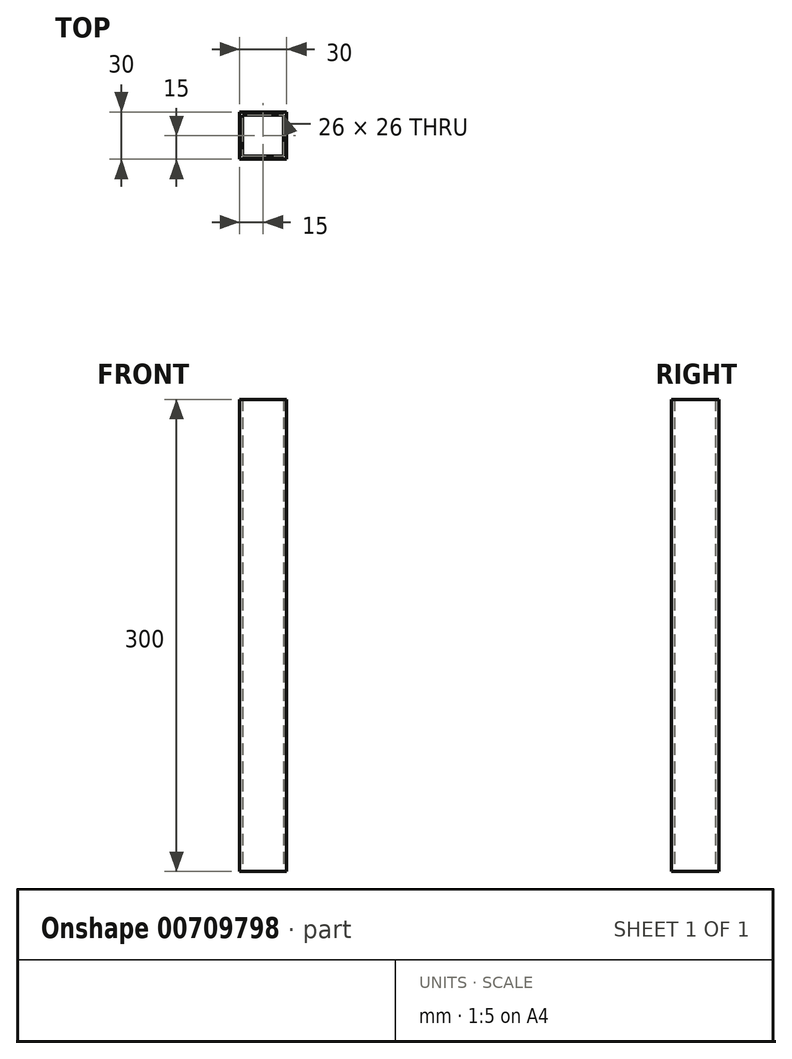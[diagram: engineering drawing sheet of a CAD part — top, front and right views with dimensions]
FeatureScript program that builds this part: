
annotation { "Feature Type Name" : "Feature", "Feature Type Description" : "" }
export const myFeature = defineFeature(function(context is Context, id is Id, definition is map)
    precondition{}
    {
        {
            var Q0;
            Q0=qCreatedBy(makeId("Top.planeOp"),FACE);
            var sketch = newSketch(context, id + "F0", { "sketchPlane" : qUnion([Q0])});
            skLineSegment(sketch, "E0.bottom", {"start": v(0, 0) * mm, "end": v(-30, 0) * mm});
            skLineSegment(sketch, "E0.top", {"start": v(0, 30) * mm, "end": v(-30, 30) * mm});
            skLineSegment(sketch, "E0.left", {"start": v(0, 0) * mm, "end": v(0, 30) * mm});
            skLineSegment(sketch, "E0.right", {"start": v(-30, 0) * mm, "end": v(-30, 30) * mm});
            skLineSegment(sketch, "E1.0", {"start": v(-28, 2) * mm, "end": v(-28, 28) * mm});
            skLineSegment(sketch, "E1.1", {"start": v(-2, 2) * mm, "end": v(-28, 2) * mm});
            skLineSegment(sketch, "E1.2", {"start": v(-2, 2) * mm, "end": v(-2, 28) * mm});
            skLineSegment(sketch, "E1.3", {"start": v(-2, 28) * mm, "end": v(-28, 28) * mm});
            skSolve(sketch);
        }
        {
            var Q0;
            Q0=makeQuery(id+"F0.imprint","IMPRINT",FACE,{"disambiguationData":[TD([[makeQuery(id+"F0.imprint","IMPRINT",EDGE,{"derivedFrom":sQuery(id+"F0.wireOp",EDGE,"E0.bottom")}),-1.0]])]});
            extrude(context, id + "F1", {"entities" : qUnion([Q0]), "depth" : 300 * mm, "offsetDistance" : 25 * mm});
        }
    });
